# Revit family: Building-IEC309Connections-GEWISS-66IB-INTERLOCKED-SOCKET-OUTLETS-HD_IP66_WITH_BOTTOM_24V
name_source: partatom
category: Apparecchi elettrici
revit_build: Autodesk Revit 2016 (Build: 20161004_0715(x64)
units: mm (PartAtom-declared; Revit-internal decimal feet)

## family parameters
Condiviso = No
Host = Muro
Mantenere orientamento annotazione = Sì
Numero OmniClass = 23.80.50.14
Punto di calcolo locali = No
Quota connettore circolare = Usa diametro
Sempre verticale = Sì
Taglio con vuoti quando caricato = No
Tipo di parte = Normale
Titolo OmniClass = Plug Connectors

## types (1)
- Building-IEC309Connections-GEWISS-66IB-INTERLOCKED-SOCKET-OUTLETS-HD_IP66_WITH_BOTTOM_24V
    Altezza da terra = 1128 mm
    Carico apparente = 0 VA
    Catalogue = BUILDING
    Catalogue Range = 66 IB
    Classificazione carico = Altro
    Colour = Violet
    Colour: = Violet
    Descrizione = VR. S.-OUT. WB. 2P 160VA TF. 230/24V CBF
    EAN code = 8011564184121
    Electrocod = 2222
    Frequency = 50Hz
    Glow Wire Test = 850 °C
    Glow wire test: = 850 °C
    IDF = 706a5ebe-ff9d-462f-b53a-49af0794706a
    IDT = 2d669e67-5247-4248-86bf-ba56704f2efd
    IP degree = IP66
    Immagine tipo = GW66998.jpg
    Impact resistance at -20 °C = 20J
    Modello = GW66998
    No. of poles = 2P
    Number of poles = 2P
    Numero poli = 2
    Operating temperature: = -25 +40 °C
    Output voltage = 20-25 V
    Potenza = 24 V
    Power = 160VA
    Presa = GEWISS - VIOLA
    Produttore = GEWISS S.p.A.
    Protection = Safety transformer
    Rated current (A) = 16
    Rated current (In) = 16
    Rated frequency (Hz) = 50Hz
    Rated power = 160VA
    SEO = Socket outlet
    Shock resistance = > IK10
    Struttura = GEWISS - Grigio RAL - 7035
    Struttura alta = GEWISS -BLU
    Technical sheet = https://www.gewiss.com
    Thermo-pressure with ball = 80
    Type of fuse = Ø 10.3x38 mm
    Type of use = Heavy duty
    Typology = Vertical
    URL = https://www.gewiss.com
    Version file RFA = 18.0
    Vetro = Vetro
    With back-mounting box = Yes
    Working temperature = -25 ÷ +40 °C

note: source unit labels omitted for Thermo-pressure with ball — the stored unit's dimension contradicts the parameter name (converter mislabeling)

## geometry (parser evidence)
native form markers: Blend x2, Sweep x2
no freeform markers — native parametric forms only
